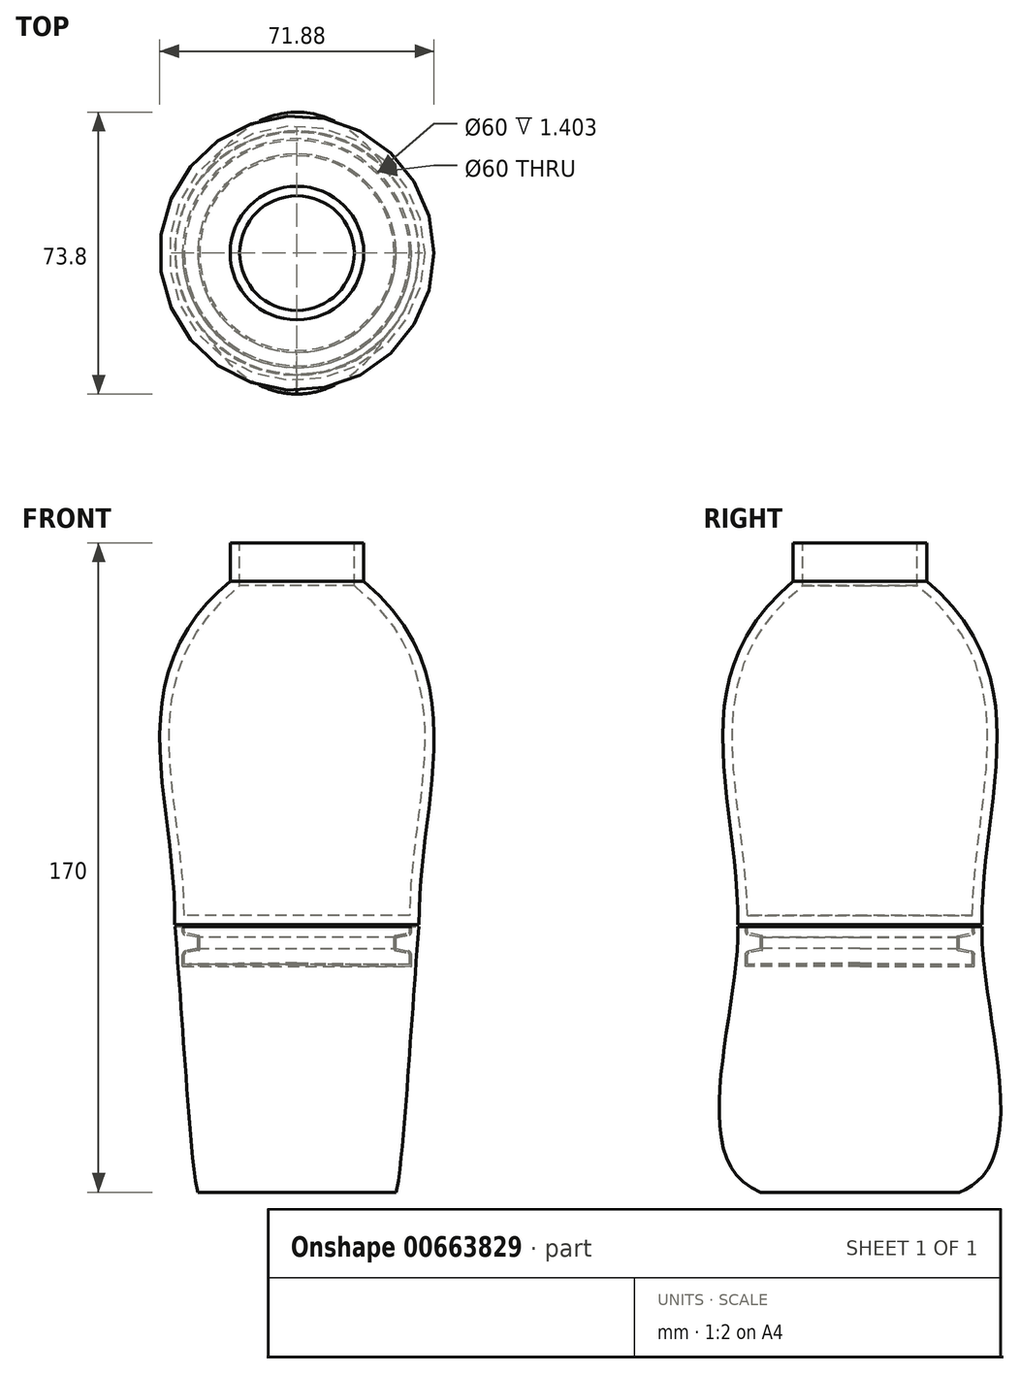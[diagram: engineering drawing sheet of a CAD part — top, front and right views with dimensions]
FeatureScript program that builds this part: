
annotation { "Feature Type Name" : "Feature", "Feature Type Description" : "" }
export const myFeature = defineFeature(function(context is Context, id is Id, definition is map)
    precondition{}
    {
        {
            var Q0;
            Q0=qCreatedBy(makeId("Right.planeOp"),FACE);
            var sketch = newSketch(context, id + "F0", { "sketchPlane" : qUnion([Q0])});
            skLineSegment(sketch, "E0", {"start": v(0, 100) * mm, "end": v(0, -100) * mm, "construction": true});
            skLineSegment(sketch, "E1", {"start": v(0, 100) * mm, "end": v(-17.5, 100) * mm});
            skLineSegment(sketch, "E2", {"start": v(-17.5, 100) * mm, "end": v(-17.5, 90) * mm});
            skLineSegment(sketch, "E3", {"start": v(0, 0) * mm, "end": v(-32, 0) * mm});
            skFitSpline(sketch, "E4", {"points": [v(-17.5, 90) * mm, v(-35.64, 41.32) * mm, v(-32, 0) * mm], "startDerivative": vector(-103.03, -85.86) * mm, "endDerivative": vector(-0.92, -92.59) * mm});
            skLineSegment(sketch, "E5", {"start": v(0, 100) * mm, "end": v(0, 0) * mm});
            skSolve(sketch);
        }
        {
            var Q0;
            Q0 = qSketchRegion(id + "F0", true);
            var Q1;
            Q1=sQuery(id+"F0.wireOp",EDGE,"E0");
            revolve(context, id + "F1", {"entities" : qUnion([Q0]), "axis" : qUnion([Q1]), "revolveType" : RevolveType.FULL});
        }
        {
            var Q0;
            Q0=makeQuery(id+"F1.opRevolve","SWEPT_FACE",FACE,{"disambiguationData":[OSD([sQuery(id+"F0.wireOp",EDGE,"E1")])]});
            shell(context, id + "F2", {"entities" : qUnion([Q0]), "thickness" : 2.5 * mm});
        }
        {
            var Q0;
            Q0=qCreatedBy(makeId("Front.planeOp"),FACE);
            var sketch = newSketch(context, id + "F3", { "sketchPlane" : qUnion([Q0])});
            skLineSegment(sketch, "E6", {"start": v(0, 0) * mm, "end": v(0, -10) * mm, "construction": true});
            skLineSegment(sketch, "E7", {"start": v(29.5, -10.3) * mm, "end": v(29.5, -7.87) * mm});
            skLineSegment(sketch, "E8", {"start": v(29.04, -7.31) * mm, "end": v(25.66, -6.67) * mm});
            skLineSegment(sketch, "E9", {"start": v(25.5, -6.47) * mm, "end": v(25.5, -3.05) * mm});
            skLineSegment(sketch, "E10", {"start": v(25.66, -2.86) * mm, "end": v(29.34, -2.1) * mm});
            skLineSegment(sketch, "E11", {"start": v(29.5, -1.9) * mm, "end": v(29.5, 0) * mm});
            skLineSegment(sketch, "E12", {"start": v(0, -10) * mm, "end": v(29.5, -10.3) * mm});
            skPoint(sketch, "E13.visualSharp", {"position": v(29.5, -7.4) * mm});
            skArc(sketch, "E13.filletArc", {"start": v(29.5, -7.87) * mm, "mid": v(29.37, -7.5) * mm, "end": v(29.04, -7.31) * mm});
            skPoint(sketch, "E14.visualSharp", {"position": v(25.5, -6.64) * mm});
            skArc(sketch, "E14.filletArc", {"start": v(25.5, -6.47) * mm, "mid": v(25.55, -6.6) * mm, "end": v(25.66, -6.67) * mm});
            skPoint(sketch, "E15.visualSharp", {"position": v(25.5, -2.89) * mm});
            skArc(sketch, "E15.filletArc", {"start": v(25.66, -2.86) * mm, "mid": v(25.54, -2.93) * mm, "end": v(25.5, -3.05) * mm});
            skPoint(sketch, "E16.visualSharp", {"position": v(29.5, -2.07) * mm});
            skArc(sketch, "E16.filletArc", {"start": v(29.34, -2.1) * mm, "mid": v(29.46, -2.03) * mm, "end": v(29.5, -1.9) * mm});
            skLineSegment(sketch, "E17", {"start": v(0, 0) * mm, "end": v(0, -10) * mm});
            skLineSegment(sketch, "E18", {"start": v(0, 0) * mm, "end": v(29.5, 0) * mm});
            skSolve(sketch);
        }
        {
            var Q0;
            Q0 = qSketchRegion(id + "F3", true);
            var Q1;
            Q1=sQuery(id+"F3.wireOp",EDGE,"E17");
            revolve(context, id + "F4", {"operationType" : NewBodyOperationType.ADD, "entities" : qUnion([Q0]), "axis" : qUnion([Q1]), "revolveType" : RevolveType.FULL});
        }
        {
            var Q0;
            Q0=makeQuery(id+"F1.opRevolve","SWEPT_FACE",FACE,{"disambiguationData":[OSD([sQuery(id+"F0.wireOp",EDGE,"E3")])]});
            cPlane(context, id + "F5", {"entities" : qUnion([Q0]), "cplaneType" : CPlaneType.OFFSET, "offset" : 0.2 * mm, "width" : 150 * mm, "height" : 150 * mm});
        }
        {
            var Q0;
            Q0=qCreatedBy(id+"F5.planeOp",FACE);
            var sketch = newSketch(context, id + "F6", { "sketchPlane" : qUnion([Q0])});
            skCircle(sketch, "E19.0", {"center": v(0, 0) * mm, "radius": 32 * mm});
            skSolve(sketch);
        }
        {
            var Q0;
            Q0=qCreatedBy(makeId("Top.planeOp"),FACE);
            cPlane(context, id + "F7", {"entities" : qUnion([Q0]), "cplaneType" : CPlaneType.OFFSET, "offset" : 70 * mm, "oppositeDirection" : true, "width" : 150 * mm, "height" : 150 * mm});
        }
        {
            var Q0;
            Q0=qCreatedBy(id+"F7.planeOp",FACE);
            var sketch = newSketch(context, id + "F8", { "sketchPlane" : qUnion([Q0])});
            skCircle(sketch, "E20", {"center": v(0, 0) * mm, "radius": 26 * mm});
            skSolve(sketch);
        }
        {
            var Q0;
            Q0=qCreatedBy(makeId("Right.planeOp"),FACE);
            var sketch = newSketch(context, id + "F9", { "sketchPlane" : qUnion([Q0])});
            skFitSpline(sketch, "E21", {"points": [v(-32, -0.2) * mm, v(-26, -70) * mm], "startDerivative": vector(1.9, -68.87) * mm, "endDerivative": vector(62.32, -23.31) * mm});
            skLineSegment(sketch, "E22", {"start": v(0, 0) * mm, "end": v(0, -70.25) * mm, "construction": true});
            skFitSpline(sketch, "E23.MirrorCS", {"points": [v(32, -0.2) * mm, v(26, -70) * mm], "startDerivative": vector(-1.9, -68.87) * mm, "endDerivative": vector(-62.32, -23.31) * mm});
            skSolve(sketch);
        }
        {
            var Q1;
            Q1 = qSketchRegion(id + "F6", true);
            var Q2;
            Q2 = qSketchRegion(id + "F8", true);
            var Q3;
            Q3=sQuery(id+"F9.wireOp",EDGE,"E21");
            var Q4;
            Q4=sQuery(id+"F9.wireOp",EDGE,"E23.MirrorCS");
            loft(context, id + "F10", {"addGuides" : true, "sheetProfilesArray" : [{ "sheetProfileEntities" : qUnion([Q1]) }, { "sheetProfileEntities" : qUnion([Q2]) }], "guidesArray" : [{ "guideEntities" : qUnion([Q3]), "guideDerivativeType" : LoftGuideDerivativeType.DEFAULT, "guideDerivativeMagnitude" : 1 }, { "guideEntities" : qUnion([Q4]), "guideDerivativeType" : LoftGuideDerivativeType.DEFAULT, "guideDerivativeMagnitude" : 1 }]});
        }
        {
            var Q0;
            Q0=makeQuery(id+"F1.opRevolve","SWEPT_BODY",BODY,{"disambiguationData":[OSD([sQuery(id+"F0.wireOp",EDGE,"E1"),sQuery(id+"F0.wireOp",EDGE,"E2"),sQuery(id+"F0.wireOp",EDGE,"E3"),sQuery(id+"F0.wireOp",EDGE,"E4"),sQuery(id+"F0.wireOp",EDGE,"E5")])]});
            var Q1;
            Q1=makeQuery(id+"F10.opLoft","SWEPT_BODY",BODY,{"disambiguationData":[OSD([makeQuery(id+"F6.imprint","IMPRINT",FACE,{"disambiguationData":[TD([[makeQuery(id+"F6.imprint","IMPRINT",EDGE,{"derivedFrom":sQuery(id+"F6.wireOp",EDGE,"E19.0")}),-1.0]])]}),makeQuery(id+"F8.imprint","IMPRINT",FACE,{"disambiguationData":[TD([[makeQuery(id+"F8.imprint","IMPRINT",EDGE,{"derivedFrom":sQuery(id+"F8.wireOp",EDGE,"E20")}),1.0]])]}),sQuery(id+"F9.wireOp",EDGE,"E21"),sQuery(id+"F9.wireOp",EDGE,"E23.MirrorCS")])]});
            var Q2;
            Q2=makeQuery(id+"F1.opRevolve","SWEPT_FACE",FACE,{"disambiguationData":[OSD([sQuery(id+"F0.wireOp",EDGE,"E3")])]});
            var Q3;
            Q3=makeQuery(id+"F4.opRevolve","SWEPT_FACE",FACE,{"disambiguationData":[OSD([sQuery(id+"F3.wireOp",EDGE,"E11")])]});
            var Q4;
            Q4=makeQuery(id+"F4.opRevolve","SWEPT_FACE",FACE,{"disambiguationData":[OSD([sQuery(id+"F3.wireOp",EDGE,"E16.filletArc")])]});
            var Q5;
            Q5=makeQuery(id+"F4.opRevolve","SWEPT_FACE",FACE,{"disambiguationData":[OSD([sQuery(id+"F3.wireOp",EDGE,"E10")])]});
            var Q6;
            Q6=makeQuery(id+"F4.opRevolve","SWEPT_FACE",FACE,{"disambiguationData":[OSD([sQuery(id+"F3.wireOp",EDGE,"E15.filletArc")])]});
            var Q7;
            Q7=makeQuery(id+"F4.opRevolve","SWEPT_FACE",FACE,{"disambiguationData":[OSD([sQuery(id+"F3.wireOp",EDGE,"E9")])]});
            var Q8;
            Q8=makeQuery(id+"F4.opRevolve","SWEPT_FACE",FACE,{"disambiguationData":[OSD([sQuery(id+"F3.wireOp",EDGE,"E7")])]});
            var Q9;
            Q9=makeQuery(id+"F4.opRevolve","SWEPT_FACE",FACE,{"disambiguationData":[OSD([sQuery(id+"F3.wireOp",EDGE,"E13.filletArc")])]});
            var Q10;
            Q10=makeQuery(id+"F4.opRevolve","SWEPT_FACE",FACE,{"disambiguationData":[OSD([sQuery(id+"F3.wireOp",EDGE,"E8")])]});
            var Q11;
            Q11=makeQuery(id+"F4.opRevolve","SWEPT_FACE",FACE,{"disambiguationData":[OSD([sQuery(id+"F3.wireOp",EDGE,"E14.filletArc")])]});
            var Q12;
            Q12=makeQuery(id+"F4.opRevolve","SWEPT_FACE",FACE,{"disambiguationData":[OSD([sQuery(id+"F3.wireOp",EDGE,"E12")])]});
            booleanBodies(context, id + "F11", {"operationType" : BooleanOperationType.SUBTRACTION, "tools" : qUnion([Q0]), "targets" : qUnion([Q1]), "offset" : true, "entitiesToOffset" : qUnion([Q2, Q3, Q4, Q5, Q6, Q7, Q8, Q9, Q10, Q11, Q12]), "offsetDistance" : 0.5 * mm, "keepTools" : true});
        }
    });
